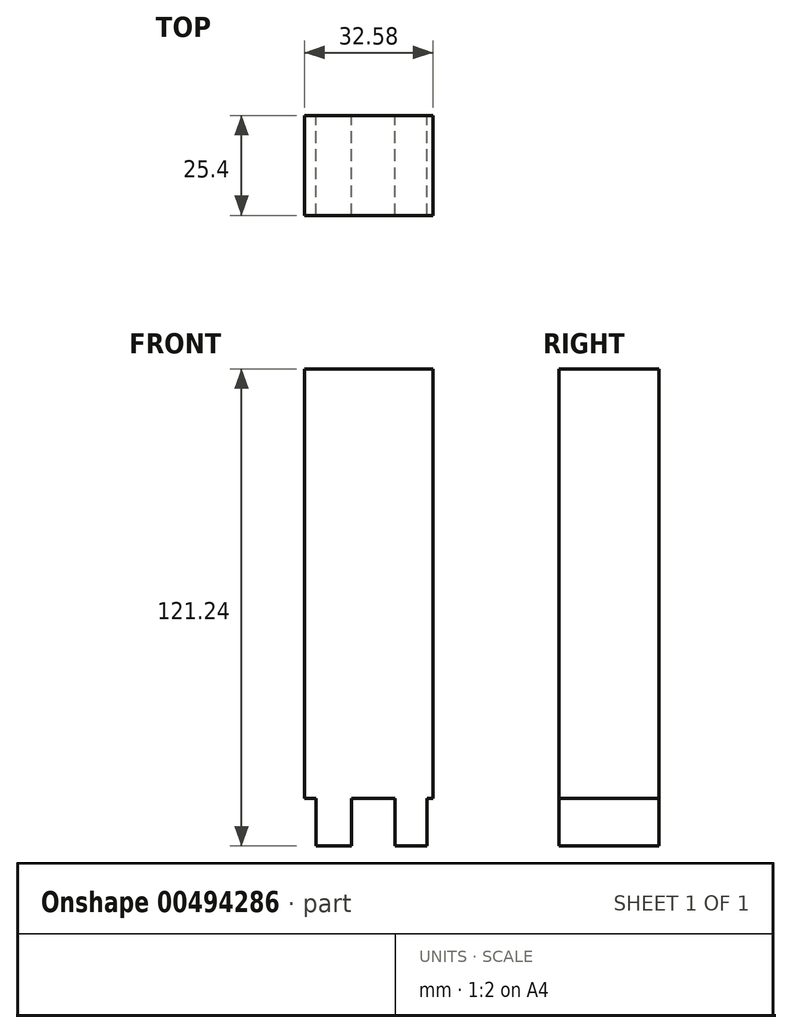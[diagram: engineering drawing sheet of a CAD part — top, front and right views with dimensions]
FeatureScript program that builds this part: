
annotation { "Feature Type Name" : "Feature", "Feature Type Description" : "" }
export const myFeature = defineFeature(function(context is Context, id is Id, definition is map)
    precondition{}
    {
        {
            var Q0;
            Q0=qCreatedBy(makeId("Front.planeOp"),FACE);
            var sketch = newSketch(context, id + "F0", { "sketchPlane" : qUnion([Q0])});
            skLineSegment(sketch, "E0.bottom", {"start": v(-23, 49.76) * mm, "end": v(9.57, 49.76) * mm});
            skLineSegment(sketch, "E0.top", {"start": v(-23, -59.33) * mm, "end": v(9.57, -59.33) * mm});
            skLineSegment(sketch, "E0.left", {"start": v(-23, 49.76) * mm, "end": v(-23, -59.33) * mm});
            skLineSegment(sketch, "E0.right", {"start": v(9.57, 49.76) * mm, "end": v(9.57, -59.33) * mm});
            skLineSegment(sketch, "E1", {"start": v(-20.16, -59.33) * mm, "end": v(-20.16, -71.48) * mm});
            skLineSegment(sketch, "E2", {"start": v(-20.16, -71.48) * mm, "end": v(-11.12, -71.48) * mm});
            skLineSegment(sketch, "E3", {"start": v(-11.12, -71.48) * mm, "end": v(-11.12, -59.33) * mm});
            skLineSegment(sketch, "E4", {"start": v(0, -59.33) * mm, "end": v(0, -71.48) * mm});
            skLineSegment(sketch, "E5", {"start": v(0, -71.48) * mm, "end": v(8.01, -71.48) * mm});
            skLineSegment(sketch, "E6", {"start": v(8.01, -71.48) * mm, "end": v(8.01, -59.33) * mm});
            skSolve(sketch);
        }
        {
            var Q0;
            Q0=makeQuery(id+"F0.imprint","IMPRINT",FACE,{"disambiguationData":[TD([[makeQuery(id+"F0.imprint","IMPRINT",EDGE,{"derivedFrom":sQuery(id+"F0.wireOp",EDGE,"E0.bottom")}),-1.0]])]});
            var Q1;
            {var subQ0=sQuery(id+"F0.wireOp",EDGE,"E1");Q1=makeQuery(id+"F0.imprint","IMPRINT",FACE,{"disambiguationData":[TD([[makeQuery(id+"F0.imprint","IMPRINT",EDGE,{"derivedFrom":subQ0}),1.0]])]});}
            var Q2;
            {var subQ0=sQuery(id+"F0.wireOp",EDGE,"E4");Q2=makeQuery(id+"F0.imprint","IMPRINT",FACE,{"disambiguationData":[TD([[makeQuery(id+"F0.imprint","IMPRINT",EDGE,{"derivedFrom":subQ0}),1.0]])]});}
            extrude(context, id + "F1", {"entities" : qUnion([Q0, Q1, Q2]), "depth" : 25.4 * mm});
        }
    });
